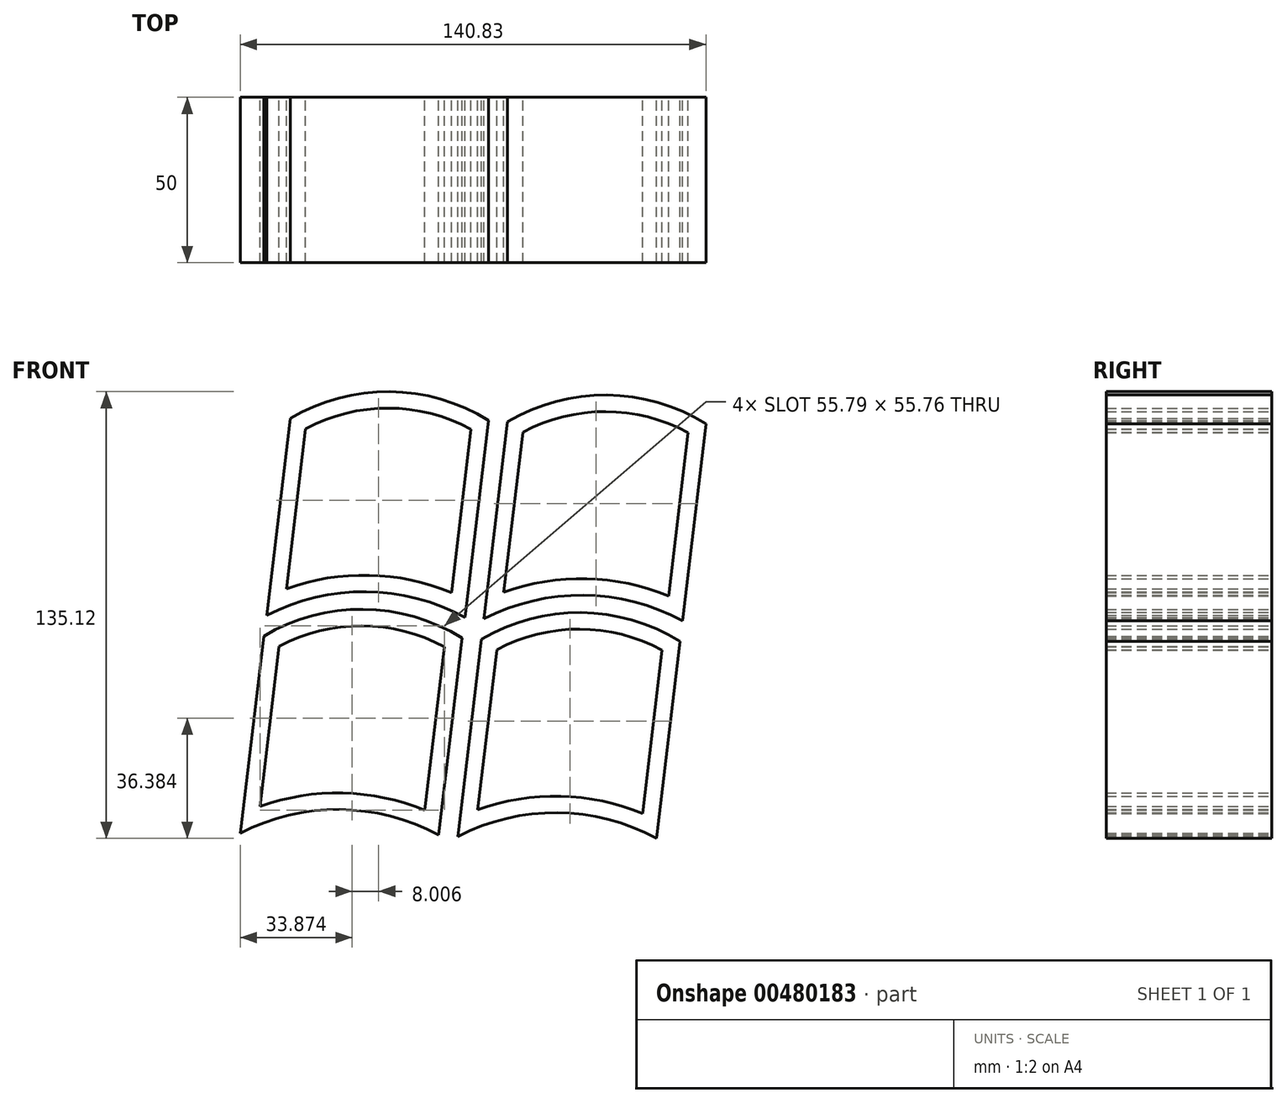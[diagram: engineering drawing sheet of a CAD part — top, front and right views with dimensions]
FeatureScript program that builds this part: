
annotation { "Feature Type Name" : "Feature", "Feature Type Description" : "" }
export const myFeature = defineFeature(function(context is Context, id is Id, definition is map)
    precondition{}
    {
        {
            var Q0;
            Q0=qCreatedBy(makeId("Front.planeOp"),FACE);
            var sketch = newSketch(context, id + "F0", { "sketchPlane" : qUnion([Q0])});
            skLineSegment(sketch, "E0", {"start": v(-112.64, 0) * mm, "end": v(-105.54, 59.58) * mm});
            skLineSegment(sketch, "E1", {"start": v(-52.64, -0.6) * mm, "end": v(-45.54, 58.99) * mm});
            skArc(sketch, "E2", {"start": v(-45.54, 58.99) * mm, "mid": v(-75.46, 67.7) * mm, "end": v(-105.54, 59.58) * mm});
            skArc(sketch, "E3", {"start": v(-52.64, -0.6) * mm, "mid": v(-82.57, 7.16) * mm, "end": v(-112.64, 0) * mm});
            skLineSegment(sketch, "E4", {"start": v(-46.92, -1.04) * mm, "end": v(-39.82, 58.54) * mm});
            skLineSegment(sketch, "E5", {"start": v(13.08, -1.63) * mm, "end": v(20.18, 57.95) * mm});
            skArc(sketch, "E6", {"start": v(20.18, 57.95) * mm, "mid": v(-9.74, 66.66) * mm, "end": v(-39.82, 58.54) * mm});
            skArc(sketch, "E7", {"start": v(13.08, -1.63) * mm, "mid": v(-16.85, 6.12) * mm, "end": v(-46.92, -1.04) * mm});
            skLineSegment(sketch, "E8", {"start": v(-120.65, -65.84) * mm, "end": v(-113.54, -6.26) * mm});
            skLineSegment(sketch, "E9", {"start": v(-60.65, -66.43) * mm, "end": v(-53.54, -6.86) * mm});
            skArc(sketch, "E10", {"start": v(-53.54, -6.86) * mm, "mid": v(-83.46, 1.85) * mm, "end": v(-113.54, -6.26) * mm});
            skArc(sketch, "E11", {"start": v(-60.65, -66.43) * mm, "mid": v(-90.58, -58.68) * mm, "end": v(-120.65, -65.84) * mm});
            skLineSegment(sketch, "E12", {"start": v(-54.8, -66.83) * mm, "end": v(-47.7, -7.25) * mm});
            skLineSegment(sketch, "E13", {"start": v(5.2, -67.42) * mm, "end": v(12.3, -7.84) * mm});
            skArc(sketch, "E14", {"start": v(12.3, -7.84) * mm, "mid": v(-17.61, 0.87) * mm, "end": v(-47.7, -7.25) * mm});
            skArc(sketch, "E15", {"start": v(5.2, -67.42) * mm, "mid": v(-24.73, -59.67) * mm, "end": v(-54.8, -66.83) * mm});
            skArc(sketch, "E16.0", {"start": v(-50.9, 56.32) * mm, "mid": v(-75.86, 62.7) * mm, "end": v(-100.87, 56.47) * mm});
            skArc(sketch, "E17.0", {"start": v(-56.79, 6.91) * mm, "mid": v(-81.6, 12.15) * mm, "end": v(-106.65, 8.06) * mm});
            skLineSegment(sketch, "E18.0", {"start": v(-106.65, 8.06) * mm, "end": v(-100.87, 56.47) * mm});
            skLineSegment(sketch, "E19.trimOffspring", {"start": v(-56.79, 6.91) * mm, "end": v(-50.9, 56.32) * mm});
            skArc(sketch, "E20.0", {"start": v(14.83, 55.28) * mm, "mid": v(-10.14, 61.66) * mm, "end": v(-35.15, 55.43) * mm});
            skLineSegment(sketch, "E21.0", {"start": v(8.94, 5.87) * mm, "end": v(14.83, 55.28) * mm});
            skArc(sketch, "E22.0", {"start": v(8.94, 5.87) * mm, "mid": v(-15.89, 11.1) * mm, "end": v(-40.93, 7.02) * mm});
            skLineSegment(sketch, "E23.0", {"start": v(-40.93, 7.02) * mm, "end": v(-35.15, 55.43) * mm});
            skArc(sketch, "E24.0", {"start": v(6.95, -10.51) * mm, "mid": v(-18.02, -4.13) * mm, "end": v(-43.03, -10.36) * mm});
            skLineSegment(sketch, "E25.0", {"start": v(1.06, -59.92) * mm, "end": v(6.95, -10.51) * mm});
            skArc(sketch, "E26.0", {"start": v(1.06, -59.92) * mm, "mid": v(-23.76, -54.68) * mm, "end": v(-48.8, -58.77) * mm});
            skLineSegment(sketch, "E27.0", {"start": v(-48.8, -58.77) * mm, "end": v(-43.03, -10.36) * mm});
            skArc(sketch, "E28.0", {"start": v(-58.9, -9.52) * mm, "mid": v(-83.87, -3.14) * mm, "end": v(-108.88, -9.37) * mm});
            skLineSegment(sketch, "E29.0", {"start": v(-64.8, -58.93) * mm, "end": v(-58.9, -9.52) * mm});
            skArc(sketch, "E30.0", {"start": v(-64.8, -58.93) * mm, "mid": v(-89.61, -53.7) * mm, "end": v(-114.65, -57.78) * mm});
            skLineSegment(sketch, "E31.0", {"start": v(-114.65, -57.78) * mm, "end": v(-108.88, -9.37) * mm});
            skSolve(sketch);
        }
        {
            var Q0;
            Q0=makeQuery(id+"F0.imprint","IMPRINT",FACE,{"disambiguationData":[TD([[makeQuery(id+"F0.imprint","IMPRINT",EDGE,{"derivedFrom":sQuery(id+"F0.wireOp",EDGE,"E0")}),-1.0]])]});
            var Q1;
            Q1=makeQuery(id+"F0.imprint","IMPRINT",FACE,{"disambiguationData":[TD([[makeQuery(id+"F0.imprint","IMPRINT",EDGE,{"derivedFrom":sQuery(id+"F0.wireOp",EDGE,"E4")}),-1.0]])]});
            var Q2;
            Q2=makeQuery(id+"F0.imprint","IMPRINT",FACE,{"disambiguationData":[TD([[makeQuery(id+"F0.imprint","IMPRINT",EDGE,{"derivedFrom":sQuery(id+"F0.wireOp",EDGE,"E12")}),-1.0]])]});
            var Q3;
            Q3=makeQuery(id+"F0.imprint","IMPRINT",FACE,{"disambiguationData":[TD([[makeQuery(id+"F0.imprint","IMPRINT",EDGE,{"derivedFrom":sQuery(id+"F0.wireOp",EDGE,"E8")}),-1.0]])]});
            extrude(context, id + "F1", {"entities" : qUnion([Q0, Q1, Q2, Q3]), "depth" : 50 * mm});
        }
    });
